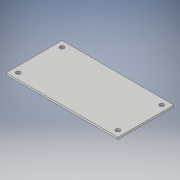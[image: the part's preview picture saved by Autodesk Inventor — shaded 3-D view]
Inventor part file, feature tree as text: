
AUTODESK INVENTOR PART (.ipt)
format: ipt  version: 2018 (Build 220112000, 112)  size: 133,632 bytes
history: native  units: in
note: dims shown in document units (in); Inventor stores cm internally (conversion verified against a paired STEP export)
features: sketch x3, extrude x3, hole x2
ambient origin geometry x8: Origin, YZ Plane, XZ Plane, XY Plane, X Axis, Y Axis, Z Axis, Center Point
bodies: Solid1 (feature_tree)
feature tree (8):
  sketch  "Sketch1"  dims[d0=7.0in d1=3.5in]
  extrude  "Extrusion1"  Depth=3.5in
  extrude  "Extrusion2"  Depth=0.9in
  sketch  "Sketch2"  dims[d2=0.9in d3=0.9in]
  hole  "Hole3"  [1 undecoded]
  extrude  "Extrusion3"  Depth=0.125in TaperAngle=0.0deg
  sketch  "Sketch4"  dims[d4=0.5in d5=2.0in d6=0.125in d7=0.0in d8=0.6in d9=0.0in d10=0.375in d11=0.375in d12=0.375in d13=0.375in d14=0.25in d15=0.375in d16=0.375in d24=0.266in d25=0.75in d26=0.375in d27=0.25in d28=0.5635in d29=1.0in d30=0.0in d31=1.0in d32=0.0in]
  hole  "Hole2"  [1 undecoded]
note: 2 required parameter values undecoded (feature->parameter linkage not recoverable at this tier; creation-order binding heuristic only, values carry confidence <= 0.55)
